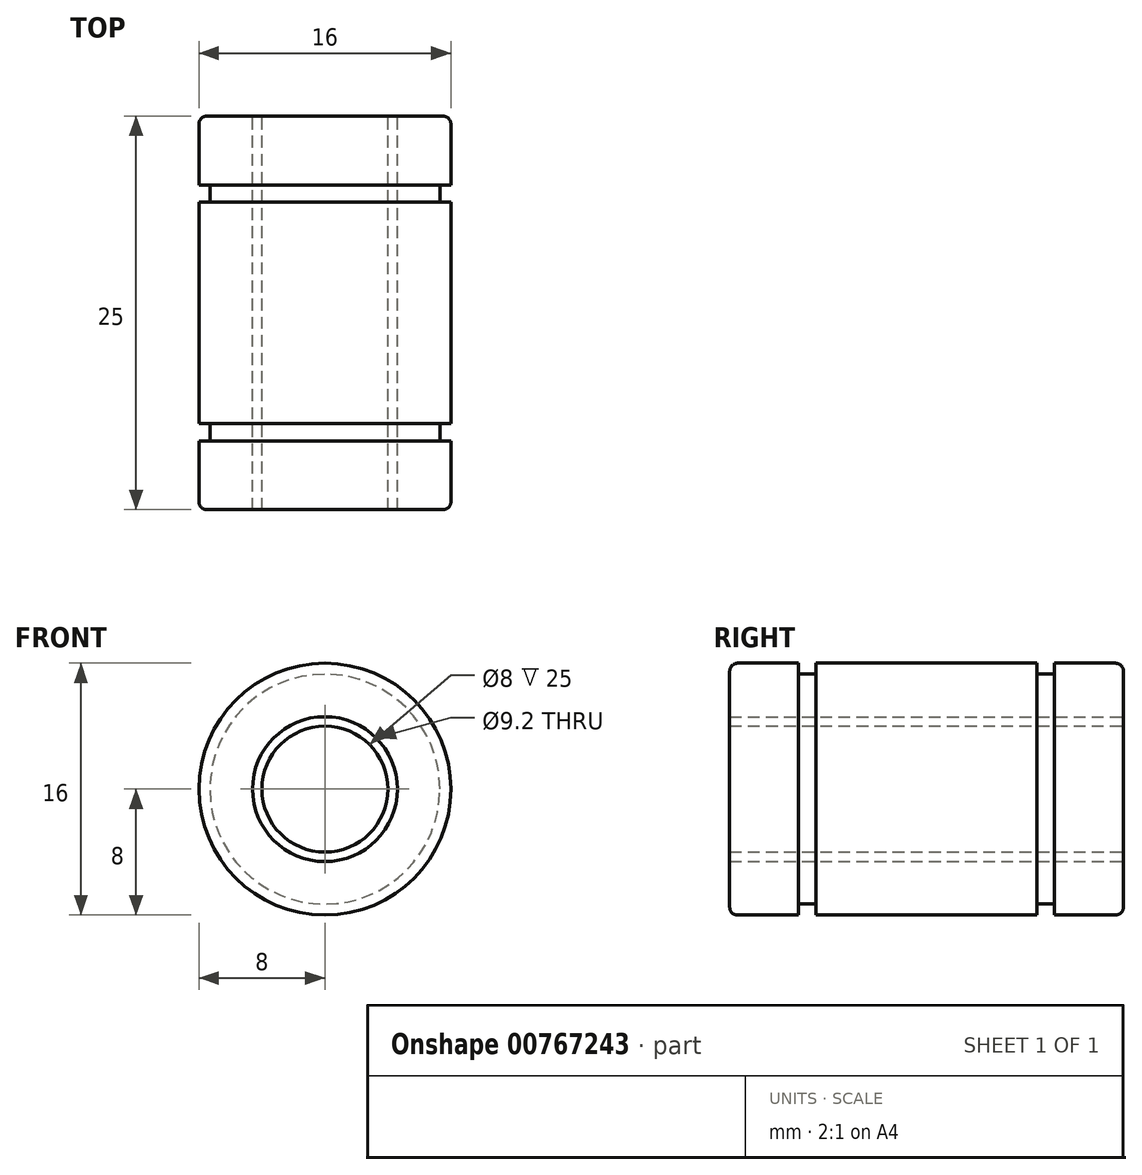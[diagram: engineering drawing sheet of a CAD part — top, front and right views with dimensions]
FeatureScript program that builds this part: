
annotation { "Feature Type Name" : "Feature", "Feature Type Description" : "" }
export const myFeature = defineFeature(function(context is Context, id is Id, definition is map)
    precondition{}
    {
        {
            var Q0;
            Q0=qCreatedBy(makeId("Front.planeOp"),FACE);
            var sketch = newSketch(context, id + "F0", { "sketchPlane" : qUnion([Q0])});
            skCircle(sketch, "E0", {"center": v(0, 0) * mm, "radius": 4 * mm});
            skCircle(sketch, "E1", {"center": v(0, 0) * mm, "radius": 8 * mm});
            skCircle(sketch, "E2.0", {"center": v(0, 0) * mm, "radius": 4.6 * mm});
            skSolve(sketch);
        }
        {
            var Q0;
            Q0=makeQuery(id+"F0.imprint","IMPRINT",FACE,{"disambiguationData":[TD([[makeQuery(id+"F0.imprint","IMPRINT",EDGE,{"derivedFrom":sQuery(id+"F0.wireOp",EDGE,"E1")}),1.0]])]});
            extrude(context, id + "F1", {"entities" : qUnion([Q0]), "endBound" : BoundingType.SYMMETRIC, "depth" : 25 * mm, "offsetDistance" : 25 * mm});
        }
        {
            var Q0;
            Q0=makeQuery(id+"F0.imprint","IMPRINT",FACE,{"disambiguationData":[TD([[makeQuery(id+"F0.imprint","IMPRINT",EDGE,{"derivedFrom":sQuery(id+"F0.wireOp",EDGE,"E0")}),-1.0]])]});
            var Q1;
            Q1=makeQuery(id+"F1.opExtrude","CAP_FACE",FACE,{"disambiguationData":[OSD([sQuery(id+"F0.wireOp",EDGE,"E1"),sQuery(id+"F0.wireOp",EDGE,"E2.0")])],"isStart":false});
            var Q2;
            Q2=makeQuery(id+"F1.opExtrude","CAP_FACE",FACE,{"disambiguationData":[OSD([sQuery(id+"F0.wireOp",EDGE,"E1"),sQuery(id+"F0.wireOp",EDGE,"E2.0")])],"isStart":true});
            extrude(context, id + "F2", {"entities" : qUnion([Q0]), "endBound" : BoundingType.UP_TO_SURFACE, "depth" : 25 * mm, "endBoundEntityFace" : qUnion([Q1]), "offsetDistance" : 25 * mm, "hasSecondDirection" : true, "secondDirectionBound" : SecondDirectionBoundingType.UP_TO_SURFACE, "secondDirectionOppositeDirection" : true, "secondDirectionDepth" : 25 * mm, "secondDirectionBoundEntityFace" : qUnion([Q2])});
        }
        {
            var Q0;
            Q0=qCreatedBy(makeId("Right.planeOp"),FACE);
            var sketch = newSketch(context, id + "F3", { "sketchPlane" : qUnion([Q0])});
            skLineSegment(sketch, "E3", {"start": v(12, -8) * mm, "end": v(-12, -8) * mm});
            skLineSegment(sketch, "E4", {"start": v(-12, 8) * mm, "end": v(12, 8) * mm});
            skLineSegment(sketch, "E5", {"start": v(-8.12, 8) * mm, "end": v(-8.12, 7.3) * mm});
            skLineSegment(sketch, "E6", {"start": v(-8.12, 7.3) * mm, "end": v(-7.03, 7.3) * mm});
            skLineSegment(sketch, "E7", {"start": v(-7.03, 7.3) * mm, "end": v(-7.03, 8) * mm});
            skLineSegment(sketch, "E8.MirrorCS", {"start": v(8.12, 7.3) * mm, "end": v(7.03, 7.3) * mm});
            skLineSegment(sketch, "E9.MirrorCS", {"start": v(7.03, 7.3) * mm, "end": v(7.03, 8) * mm});
            skLineSegment(sketch, "E10.MirrorCS", {"start": v(8.12, 8) * mm, "end": v(8.12, 7.3) * mm});
            skSolve(sketch);
        }
        {
            var Q0;
            {var subQ0=sQuery(id+"F3.wireOp",EDGE,"E5");Q0=makeQuery(id+"F3.imprint","IMPRINT",FACE,{"disambiguationData":[TD([[makeQuery(id+"F3.imprint","IMPRINT",EDGE,{"derivedFrom":subQ0}),1.0]])]});}
            var Q1;
            Q1=makeQuery(id+"F3.imprint","IMPRINT",FACE,{"disambiguationData":[TD([[makeQuery(id+"F3.imprint","IMPRINT",EDGE,{"derivedFrom":sQuery(id+"F3.wireOp",EDGE,"E8.MirrorCS")}),-1.0]])]});
            var Q2;
            Q2=makeQuery(id+"F1.opExtrude","CAP_EDGE",EDGE,{"disambiguationData":[OSD([sQuery(id+"F0.wireOp",EDGE,"E1")])],"isStart":false});
            revolve(context, id + "F4", {"operationType" : NewBodyOperationType.REMOVE, "surfaceOperationType" : NewSurfaceOperationType.NEW, "entities" : qUnion([Q0, Q1]), "axis" : qUnion([Q2]), "revolveType" : RevolveType.FULL, "oppositeDirection" : true});
        }
        {
            var Q0;
            Q0=makeQuery(id+"F1.opExtrude","CAP_EDGE",EDGE,{"disambiguationData":[OSD([sQuery(id+"F0.wireOp",EDGE,"E1")])],"isStart":false});
            var Q1;
            Q1=makeQuery(id+"F1.opExtrude","CAP_EDGE",EDGE,{"disambiguationData":[OSD([sQuery(id+"F0.wireOp",EDGE,"E1")])],"isStart":true});
            fillet(context, id + "F5", {"entities" : qUnion([Q0, Q1]), "radius" : .5 * mm, "tangentPropagation" : true, "allowEdgeOverflow" : false});
        }
    });
